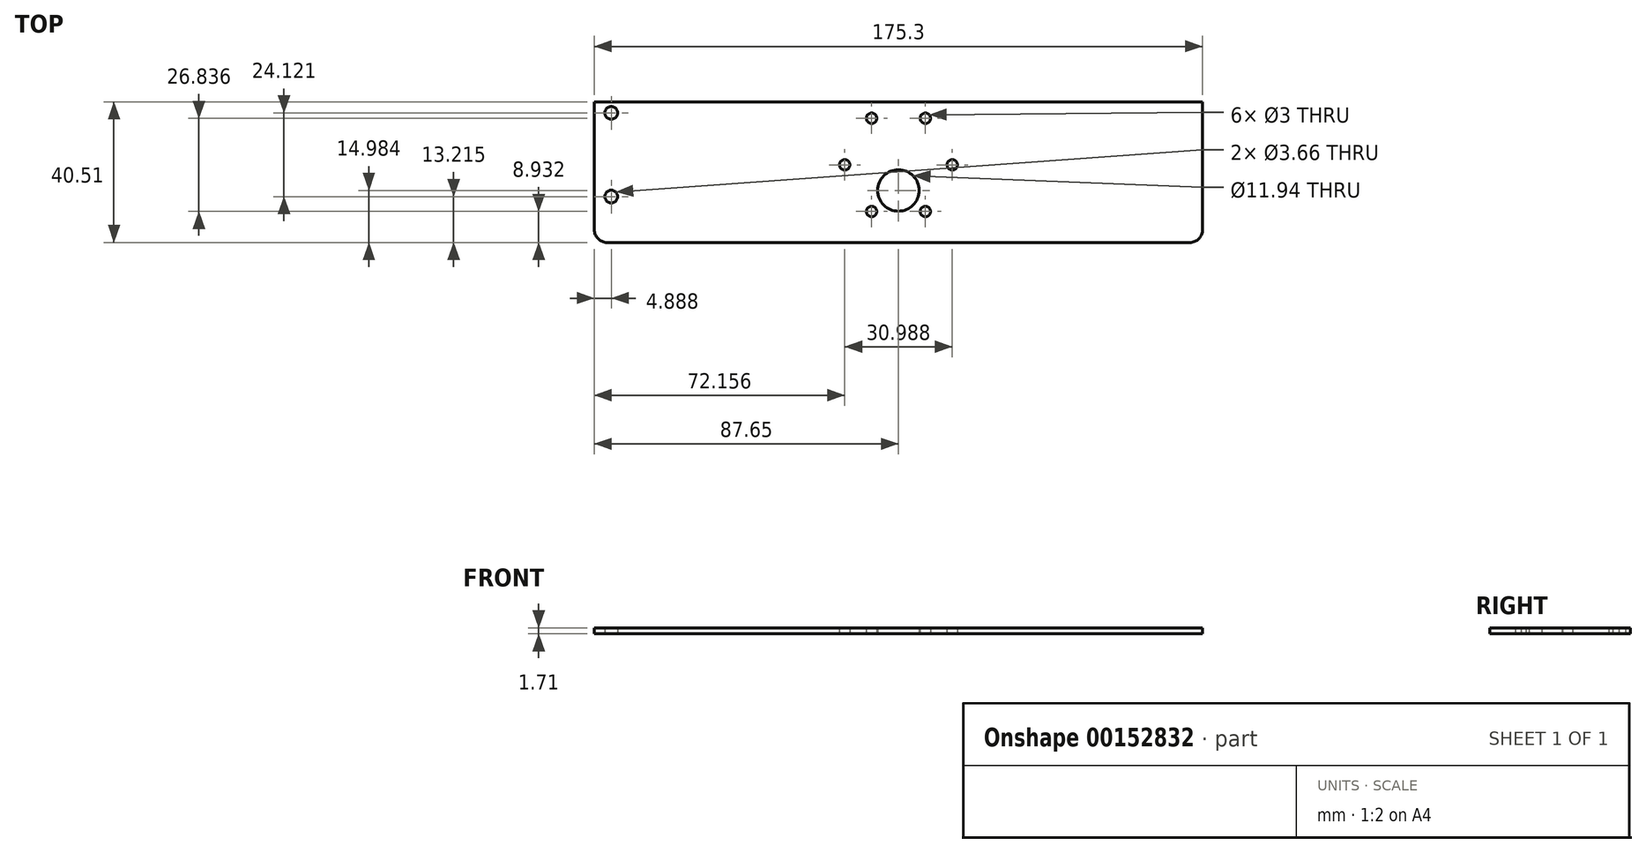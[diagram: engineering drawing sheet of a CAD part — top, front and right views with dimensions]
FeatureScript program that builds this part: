
annotation { "Feature Type Name" : "Feature", "Feature Type Description" : "" }
export const myFeature = defineFeature(function(context is Context, id is Id, definition is map)
    precondition{}
    {
        {
            var Q0;
            Q0=qCreatedBy(makeId("Top.planeOp"),FACE);
            var sketch = newSketch(context, id + "F0", { "sketchPlane" : qUnion([Q0])});
            skCircle(sketch, "E0.cCircle", {"center": v(0, 0) * mm, "radius": 13.42 * mm, "construction": true});
            skLineSegment(sketch, "E0.0", {"start": v(7.75, -13.42) * mm, "end": v(-7.75, -13.42) * mm, "construction": true});
            skLineSegment(sketch, "E0.1", {"start": v(-7.75, -13.42) * mm, "end": v(-15.5, 0) * mm, "construction": true});
            skLineSegment(sketch, "E0.2", {"start": v(-15.5, 0) * mm, "end": v(-7.75, 13.42) * mm, "construction": true});
            skLineSegment(sketch, "E0.3", {"start": v(-7.75, 13.42) * mm, "end": v(7.75, 13.42) * mm, "construction": true});
            skLineSegment(sketch, "E0.4", {"start": v(7.75, 13.42) * mm, "end": v(15.5, 0) * mm, "construction": true});
            skLineSegment(sketch, "E0.5", {"start": v(15.5, 0) * mm, "end": v(7.75, -13.42) * mm, "construction": true});
            skLineSegment(sketch, "E1.bottom", {"start": v(-87.65, 18.16) * mm, "end": v(87.65, 18.16) * mm});
            skLineSegment(sketch, "E1.top", {"start": v(-87.65, -22.35) * mm, "end": v(87.65, -22.35) * mm});
            skLineSegment(sketch, "E1.left", {"start": v(-87.65, 18.16) * mm, "end": v(-87.65, -22.35) * mm});
            skLineSegment(sketch, "E1.right", {"start": v(87.65, 18.16) * mm, "end": v(87.65, -22.35) * mm});
            skLineSegment(sketch, "E2", {"start": v(0, 0) * mm, "end": v(0, -7.37) * mm, "construction": true});
            skCircle(sketch, "E3", {"center": v(0, -7.37) * mm, "radius": 5.97 * mm});
            skCircle(sketch, "E4", {"center": v(15.5, 0) * mm, "radius": 1.5 * mm});
            skCircle(sketch, "E5", {"center": v(7.75, 13.42) * mm, "radius": 1.5 * mm});
            skCircle(sketch, "E6", {"center": v(-7.75, 13.42) * mm, "radius": 1.5 * mm});
            skCircle(sketch, "E7", {"center": v(-15.5, 0) * mm, "radius": 1.5 * mm});
            skCircle(sketch, "E8", {"center": v(-7.75, -13.42) * mm, "radius": 1.5 * mm});
            skCircle(sketch, "E9", {"center": v(7.75, -13.42) * mm, "radius": 1.5 * mm});
            skLineSegment(sketch, "E10", {"start": v(0, 0) * mm, "end": v(0, 18.16) * mm, "construction": true});
            skLineSegment(sketch, "E11", {"start": v(0, -7.37) * mm, "end": v(0, -22.35) * mm, "construction": true});
            skLineSegment(sketch, "E12", {"start": v(-82.76, 18.16) * mm, "end": v(-82.76, 14.99) * mm, "construction": true});
            skLineSegment(sketch, "E13", {"start": v(-82.76, 14.99) * mm, "end": v(-87.65, 14.99) * mm, "construction": true});
            skLineSegment(sketch, "E14", {"start": v(87.65, -7.16) * mm, "end": v(52.66, -7.16) * mm, "construction": true});
            skCircle(sketch, "E15", {"center": v(-82.76, 14.99) * mm, "radius": 1.83 * mm});
            skLineSegment(sketch, "E16", {"start": v(-82.76, 14.99) * mm, "end": v(-82.76, -9.14) * mm, "construction": true});
            skLineSegment(sketch, "E17", {"start": v(-82.76, -9.14) * mm, "end": v(-82.76, -22.35) * mm, "construction": true});
            skCircle(sketch, "E18", {"center": v(-82.76, -9.14) * mm, "radius": 1.83 * mm});
            skSolve(sketch);
        }
        {
            var Q0;
            Q0 = qSketchRegion(id + "F0", true);
            extrude(context, id + "F1", {"entities" : qUnion([Q0]), "depth" : 1.7 * mm});
        }
        {
            var Q0;
            Q0=makeQuery(id+"F1.opExtrude","SWEPT_EDGE",EDGE,{"disambiguationData":[OSD([sQuery(id+"F0.wireOp",EDGE,"E1.top"),sQuery(id+"F0.wireOp",EDGE,"E1.left")])]});
            var Q1;
            Q1=makeQuery(id+"F1.opExtrude","SWEPT_EDGE",EDGE,{"disambiguationData":[OSD([sQuery(id+"F0.wireOp",EDGE,"E1.top"),sQuery(id+"F0.wireOp",EDGE,"E1.right")])]});
            fillet(context, id + "F2", {"entities" : qUnion([Q0, Q1]), "radius" : 3.7 * mm, "tangentPropagation" : true, "allowEdgeOverflow" : false});
        }
    });
